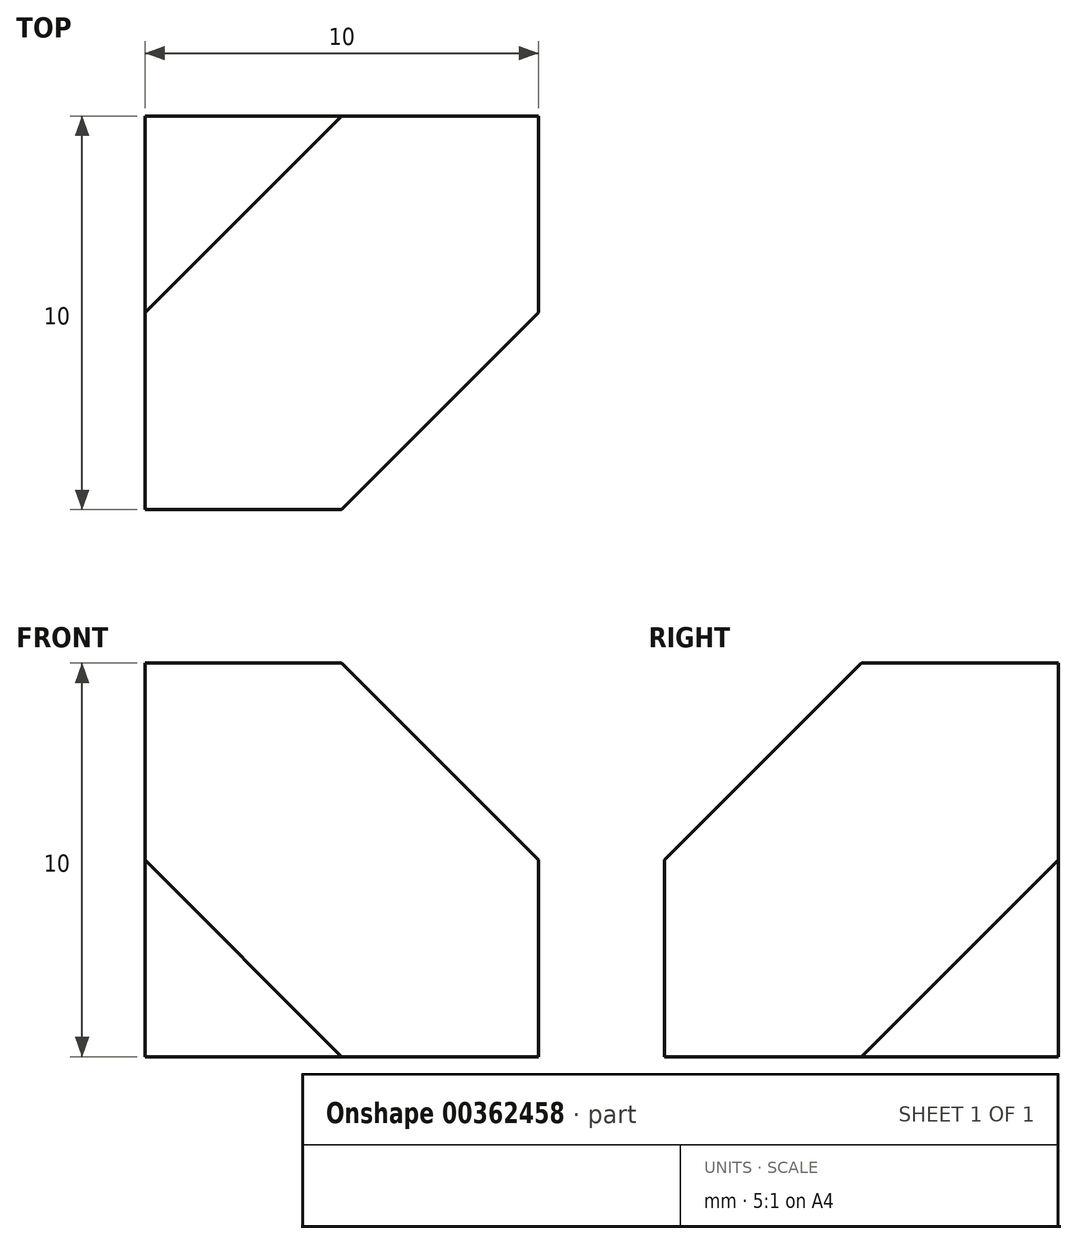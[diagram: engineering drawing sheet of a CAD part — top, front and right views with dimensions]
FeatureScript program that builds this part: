
annotation { "Feature Type Name" : "Feature", "Feature Type Description" : "" }
export const myFeature = defineFeature(function(context is Context, id is Id, definition is map)
    precondition{}
    {
        {
            var Q0;
            Q0=qCreatedBy(makeId("Front.planeOp"),FACE);
            var sketch = newSketch(context, id + "F0", { "sketchPlane" : qUnion([Q0])});
            skLineSegment(sketch, "E0.bottom", {"start": v(0, 0) * mm, "end": v(-10, 0) * mm});
            skLineSegment(sketch, "E0.top", {"start": v(0, 10) * mm, "end": v(-10, 10) * mm});
            skLineSegment(sketch, "E0.left", {"start": v(0, 0) * mm, "end": v(0, 10) * mm});
            skLineSegment(sketch, "E0.right", {"start": v(-10, 0) * mm, "end": v(-10, 10) * mm});
            skSolve(sketch);
        }
        {
            var Q0;
            Q0 = qSketchRegion(id + "F0", true);
            extrude(context, id + "F1", {"entities" : qUnion([Q0]), "depth" : 10 * mm});
        }
        {
            var Q0;
            Q0=makeQuery(id+"F1.opExtrude","CAP_FACE",FACE,{"disambiguationData":[OSD([sQuery(id+"F0.wireOp",EDGE,"E0.bottom"),sQuery(id+"F0.wireOp",EDGE,"E0.top"),sQuery(id+"F0.wireOp",EDGE,"E0.left"),sQuery(id+"F0.wireOp",EDGE,"E0.right")])],"isStart":false});
            var sketch = newSketch(context, id + "F2", { "sketchPlane" : qUnion([Q0])});
            skPoint(sketch, "E1", {"position": v(-5, 0) * mm});
            skSolve(sketch);
        }
        {
            var Q0;
            Q0=makeQuery(id+"F1.opExtrude","SWEPT_FACE",FACE,{"disambiguationData":[OSD([sQuery(id+"F0.wireOp",EDGE,"E0.left")])]});
            var sketch = newSketch(context, id + "F3", { "sketchPlane" : qUnion([Q0])});
            skPoint(sketch, "E2", {"position": v(0, 5) * mm});
            skSolve(sketch);
        }
        {
            var Q0;
            Q0=makeQuery(id+"F1.opExtrude","SWEPT_FACE",FACE,{"disambiguationData":[OSD([sQuery(id+"F0.wireOp",EDGE,"E0.top")])]});
            var sketch = newSketch(context, id + "F4", { "sketchPlane" : qUnion([Q0])});
            skPoint(sketch, "E3", {"position": v(-5, 0) * mm});
            skSolve(sketch);
        }
        {
            var Q0;
            Q0=makeQuery(id+"F1.opExtrude","CAP_FACE",FACE,{"disambiguationData":[OSD([sQuery(id+"F0.wireOp",EDGE,"E0.bottom"),sQuery(id+"F0.wireOp",EDGE,"E0.top"),sQuery(id+"F0.wireOp",EDGE,"E0.left"),sQuery(id+"F0.wireOp",EDGE,"E0.right")])],"isStart":true});
            var sketch = newSketch(context, id + "F5", { "sketchPlane" : qUnion([Q0])});
            skLineSegment(sketch, "E4", {"start": v(5, 10) * mm, "end": v(0, 5) * mm});
            skSolve(sketch);
        }
        {
            var Q0;
            Q0=makeQuery(id+"F1.opExtrude","CAP_EDGE",EDGE,{"disambiguationData":[OSD([sQuery(id+"F0.wireOp",EDGE,"E0.top")])],"isStart":true});
            cPoint(context, id + "F6", {"entities" : qUnion([Q0]), "parameter" : 0.5});
        }
        {
            var Q0;
            Q0 = qCreatedBy(id + "F6" ,VERTEX);
            var Q1;
            Q1=sQuery(id+"F3.wireOp",VERTEX,"E2");
            var Q2;
            Q2=sQuery(id+"F2.wireOp",VERTEX,"E1");
            cPlane(context, id + "F7", {"entities" : qUnion([Q0, Q1, Q2]), "cplaneType" : CPlaneType.THREE_POINT, "offset" : 25 * mm, "width" : 150 * mm, "height" : 150 * mm});
        }
        {
            var Q0;
            {var subQ0=sQuery(id+"F0.wireOp",EDGE,"E0.top");Q0=makeQuery(id+"F4.imprint","IMPRINT",FACE,{"disambiguationData":[TD([[makeQuery(id+"F4.imprint","IMPRINT",EDGE,{"derivedFrom":makeQuery(id+"F1.opExtrude","CAP_EDGE",EDGE,{"disambiguationData":[OSD([subQ0])],"isStart":true})}),1.0]])]});}
            var Q1;
            Q1=qCreatedBy(id+"F7.planeOp",FACE);
            extrude(context, id + "F8", {"entities" : qUnion([Q0]), "operationType" : NewBodyOperationType.REMOVE, "endBound" : BoundingType.UP_TO_SURFACE, "oppositeDirection" : true, "endBoundEntityFace" : qUnion([Q1]), "depth" : 25 * mm});
        }
    });
